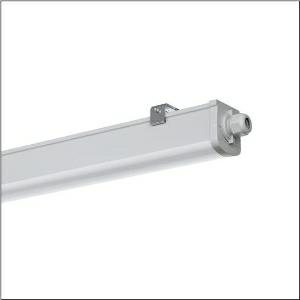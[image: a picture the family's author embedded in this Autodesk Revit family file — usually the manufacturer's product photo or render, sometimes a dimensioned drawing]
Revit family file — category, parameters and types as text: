
# Revit family: monsun_r__31_51fa207k430b_6f38
name_source: partatom
category: Lighting Fixtures
units: mm (PartAtom-declared; Revit-internal decimal feet)

## family parameters
Cut with Voids When Loaded = No
Host = Face
Light Source = No
Part Type = Normal
Room Calculation Point = No
Round Connector Dimension = Use Diameter
Shared = No

## types (1)
- Monsun® 31 (1 x LED, 3000 lm, 22 W, 4000K)
    Apparent Load = 22 VA
    CIE Flux Codes = 42 72 91 92 100
    Color Rendering = 80
    Color Temperature = 4000K
    Default Elevation = 1800 mm
    Description = Monsun® 31, damp-proof luminaire, primary optical cover: diffuser, of PC, frosted, light emission: direct distribution, primary light characteristic: symmetric, installation type: surface-mounted, LED, rated luminous flux: 3.000lm, luminous efficacy: 136lm/W, light colour: 840, colour temperature: 4000K, control gear: ON/OFF, with terminal, 3+1-pole, max. 2.5mm², through-wiring: 3x 2.5mm² + 1x 1.5mm², mains connection: 220..240V, AC, 50/60Hz, rated input power: 22W, housing, luminaire housing, of PC, light grey (RAL 7035), length: 1.158mm, width: 68mm, height: 76mm, protection rating (complete): IP66, insulation class (complete): insulation class II (safety insulation), certification: CE, ENEC, UKCA, protection symbol: D, impact resistance: IK08, permissible operating ambient temperature: -20..+40°C, corresponds to IFS (International Featured Standards) requirements for safety and quality in the food industry, contact your sales advisor before using the luminaires in applications with unclear chemical exposure, large temperature fluctuations or condensation-forming humidity, packaging unit: 1 piece
    Height = 77 mm
    Lamp = 1 x LED
    Lamp Light Flux = 3000 lm
    Lamp Power = 22 W
    Lamp count = 1
    Length = 1218 mm
    Luminous efficacy = 136 lm/W
    Manufacturer = Siteco
    ModVariant = No
    Model = 51FA207K430B
    Mounting Place = Ceiling
    Mounting Type = Surface mounted
    Number of Poles = 1
    OnlyDefault = Yes
    Power Factor = 1
    Product Name = Monsun® 31
    Product group = damp-proof luminaire
    ProductGroupID = 301
    Protection Class = Protection class II
    Protection Degree = IP 66
    RLX_Detail_Level = 1
    RLX_Emergency_Light_Flux = 0 lm
    RLX_Emergency_Type = 0
    RLX_Emergency_Type_DB = No
    RlxData = <blob elided: 33001 chars, md5=f0741fb1>
    Socket = socket
    Standby Power = 0 W
    System Light Flux = 3000 lm
    System Power = 22 W
    Type Comments = Product without accessories
    Type Image = l_1006174.jpg
    URL = http://relux.com
    VarID = ---
    Voltage = 0 V
    Weight = 0.00 kg
    Width = 69 mm

## geometry (parser evidence)
native form markers: Blend x4, Sweep x9
no freeform markers — native parametric forms only
